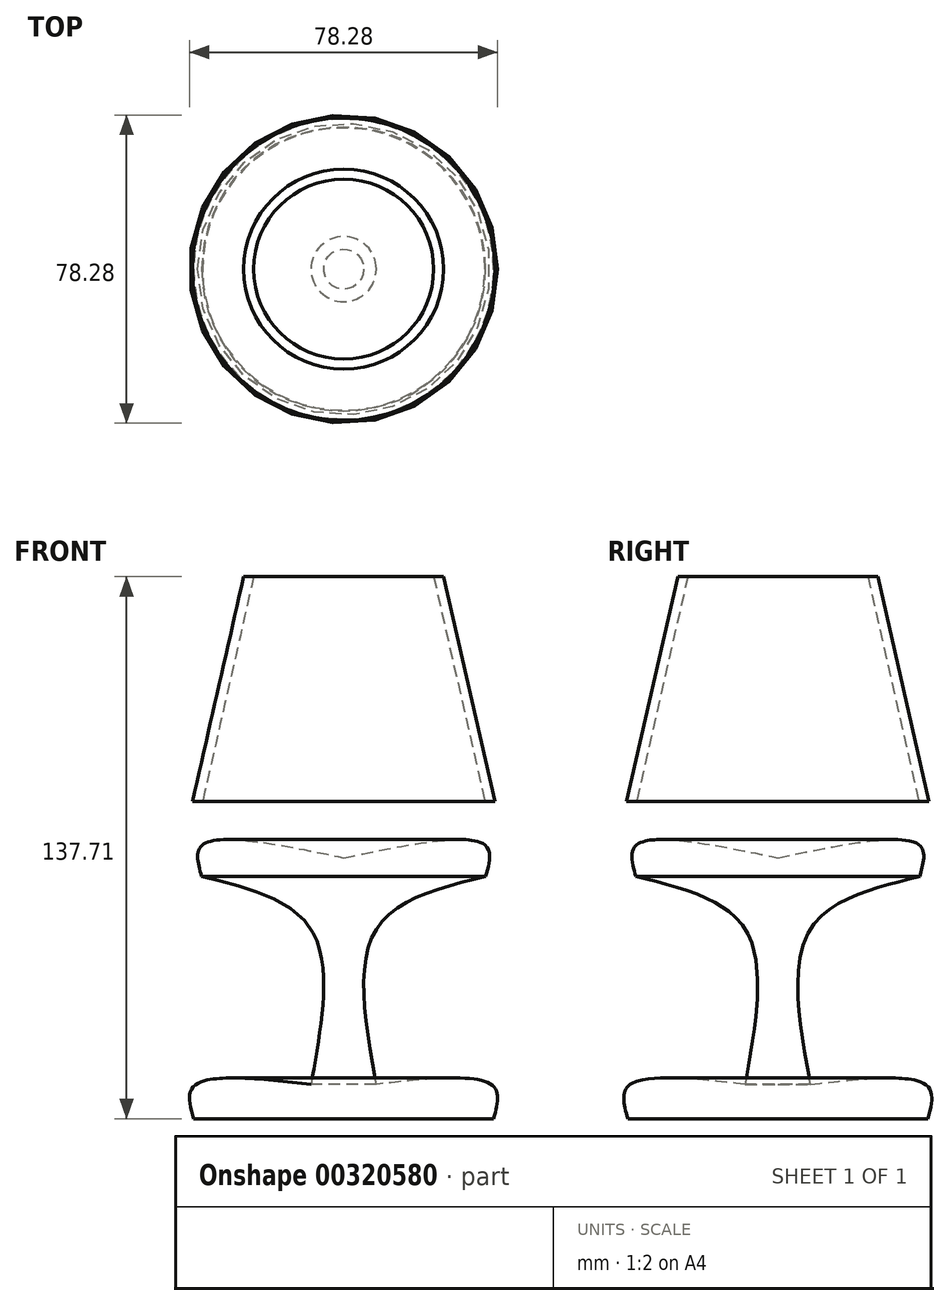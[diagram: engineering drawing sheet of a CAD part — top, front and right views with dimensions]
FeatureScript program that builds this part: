
annotation { "Feature Type Name" : "Feature", "Feature Type Description" : "" }
export const myFeature = defineFeature(function(context is Context, id is Id, definition is map)
    precondition{}
    {
        {
            var Q0;
            Q0=qCreatedBy(makeId("Front.planeOp"),FACE);
            var sketch = newSketch(context, id + "F0", { "sketchPlane" : qUnion([Q0])});
            skLineSegment(sketch, "E0", {"start": v(0, -61.5) * mm, "end": v(-38.1, -61.5) * mm});
            skFitSpline(sketch, "E1", {"points": [v(-38.1, -61.5) * mm, v(-38.1, -53.3) * mm, v(-8.3, -52.78) * mm], "startDerivative": vector(-7.82, 27.83) * mm, "endDerivative": vector(60.34, -6.77) * mm});
            skFitSpline(sketch, "E2", {"points": [v(-8.3, -52.78) * mm, v(-8.3, -13.36) * mm, v(-36.05, 0) * mm], "startDerivative": vector(15.7, 86.42) * mm, "endDerivative": vector(-73.02, 17.72) * mm});
            skFitSpline(sketch, "E3", {"points": [v(-36.05, 0) * mm, v(-36.05, 7.91) * mm, v(0, 4.8) * mm], "startDerivative": vector(-8.43, 29.51) * mm, "endDerivative": vector(70.93, -14.58) * mm});
            skLineSegment(sketch, "E4", {"start": v(0, 4.8) * mm, "end": v(0, -61.5) * mm});
            skSolve(sketch);
        }
        {
            var Q0;
            Q0=makeQuery(id+"F0.imprint","IMPRINT",FACE,{"disambiguationData":[TD([[makeQuery(id+"F0.imprint","IMPRINT",EDGE,{"derivedFrom":sQuery(id+"F0.wireOp",EDGE,"E0")}),-1.0]])]});
            var Q1;
            Q1=sQuery(id+"F0.wireOp",EDGE,"E4");
            revolve(context, id + "F1", {"entities" : qUnion([Q0]), "axis" : qUnion([Q1]), "revolveType" : RevolveType.FULL});
        }
        {
            var Q0;
            Q0=qCreatedBy(makeId("Front.planeOp"),FACE);
            var sketch = newSketch(context, id + "F2", { "sketchPlane" : qUnion([Q0])});
            skLineSegment(sketch, "E5", {"start": v(0, 0) * mm, "end": v(0, 76.2) * mm, "construction": true});
            skLineSegment(sketch, "E6", {"start": v(0, 76.2) * mm, "end": v(-25.4, 76.2) * mm, "construction": true});
            skLineSegment(sketch, "E7", {"start": v(0, 0) * mm, "end": v(0, 19.05) * mm, "construction": true});
            skLineSegment(sketch, "E8", {"start": v(0, 19.05) * mm, "end": v(-38.41, 19.05) * mm, "construction": true});
            skLineSegment(sketch, "E9", {"start": v(-38.41, 19.05) * mm, "end": v(-35.87, 19.05) * mm, "construction": true});
            skLineSegment(sketch, "E10", {"start": v(-25.4, 76.2) * mm, "end": v(-22.86, 76.2) * mm, "construction": true});
            skLineSegment(sketch, "E11", {"start": v(-25.4, 76.2) * mm, "end": v(-22.86, 76.2) * mm});
            skLineSegment(sketch, "E12", {"start": v(-38.41, 19.05) * mm, "end": v(-25.4, 76.2) * mm});
            skLineSegment(sketch, "E13", {"start": v(-22.86, 76.2) * mm, "end": v(-35.87, 19.05) * mm});
            skLineSegment(sketch, "E14", {"start": v(-35.87, 19.05) * mm, "end": v(-38.41, 19.05) * mm});
            skSolve(sketch);
        }
        {
            var Q0;
            Q0=makeQuery(id+"F2.imprint","IMPRINT",FACE,{"disambiguationData":[TD([[makeQuery(id+"F2.imprint","IMPRINT",EDGE,{"derivedFrom":sQuery(id+"F2.wireOp",EDGE,"E12")}),-1.0]])]});
            var Q1;
            Q1=sQuery(id+"F2.wireOp",EDGE,"E5");
            revolve(context, id + "F3", {"entities" : qUnion([Q0]), "axis" : qUnion([Q1]), "revolveType" : RevolveType.FULL});
        }
    });
